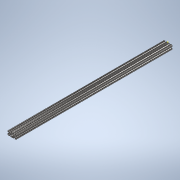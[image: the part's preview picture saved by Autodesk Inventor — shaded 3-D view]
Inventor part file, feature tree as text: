
AUTODESK INVENTOR PART (.ipt)
format: ipt  version: 2020 (Build 240168000, 168)  size: 362,496 bytes
history: native  units: in
note: dims shown in document units (in); Inventor stores cm internally (conversion verified against a paired STEP export)
features: sketch x2, extrude x1
ambient origin geometry x8: Origin, YZ Plane, XZ Plane, XY Plane, X Axis, Y Axis, Z Axis, Center Point
bodies: Solid1 (feature_tree)
feature tree (3):
  extrude  "Extrusion1"  [1 undecoded]
  sketch  "Sketch2"
  sketch  "Sketch1"  dims[d0=37.0in d1=0.0in]
note: 1 required parameter value undecoded (feature->parameter linkage not recoverable at this tier; creation-order binding heuristic only, values carry confidence <= 0.55)
